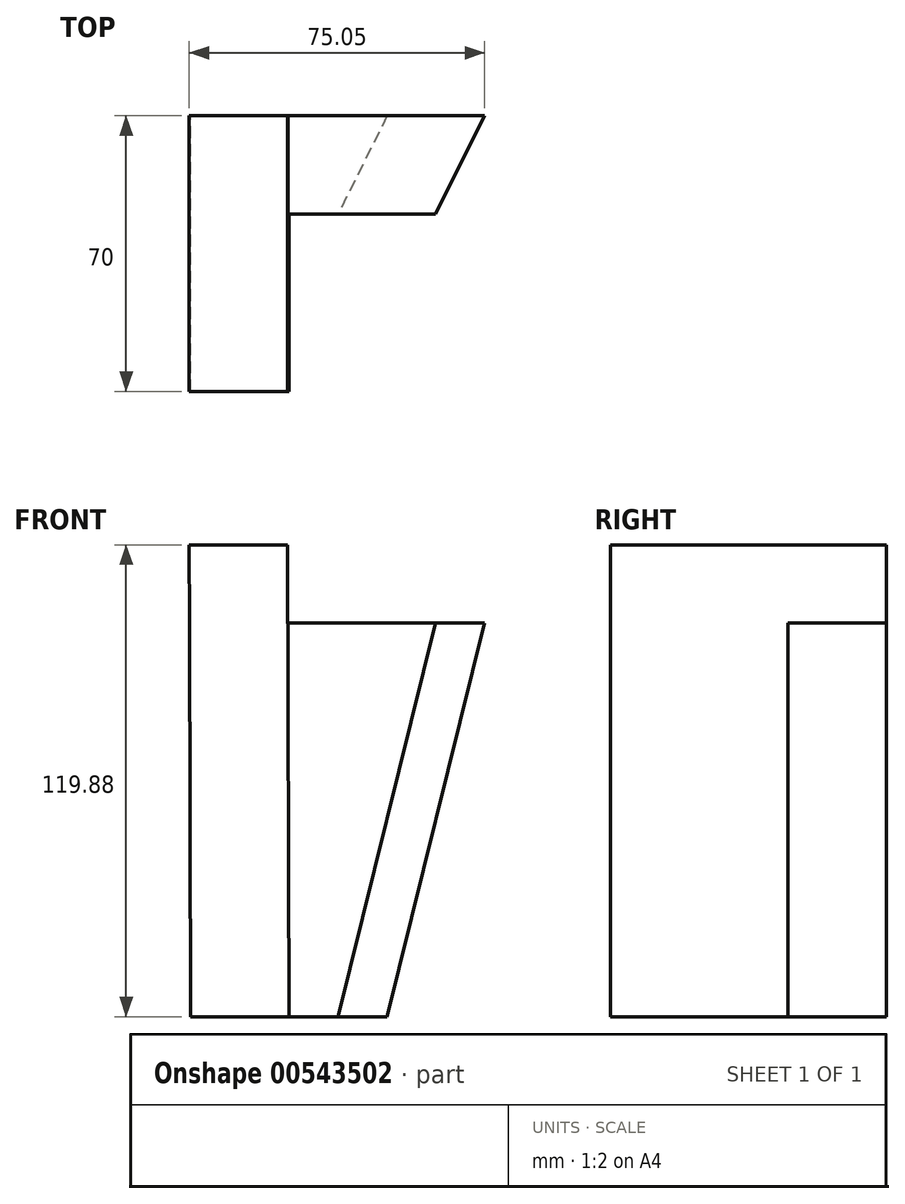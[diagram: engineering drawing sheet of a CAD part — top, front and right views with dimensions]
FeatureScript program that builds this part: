
annotation { "Feature Type Name" : "Feature", "Feature Type Description" : "" }
export const myFeature = defineFeature(function(context is Context, id is Id, definition is map)
    precondition{}
    {
        {
            var Q0;
            Q0=qCreatedBy(makeId("Top.planeOp"),FACE);
            cPlane(context, id + "F0", {"entities" : qUnion([Q0]), "cplaneType" : CPlaneType.OFFSET, "offset" : 100 * mm, "width" : 150 * mm, "height" : 150 * mm});
        }
        {
            var Q0;
            Q0=qCreatedBy(id+"F0.planeOp",FACE);
            var sketch = newSketch(context, id + "F1", { "sketchPlane" : qUnion([Q0])});
            skLineSegment(sketch, "E0", {"start": v(-31.5, -38.33) * mm, "end": v(-31.5, 31.67) * mm});
            skLineSegment(sketch, "E1", {"start": v(-31.5, 31.67) * mm, "end": v(43.5, 31.67) * mm});
            skLineSegment(sketch, "E2", {"start": v(43.5, 31.67) * mm, "end": v(31, 6.67) * mm});
            skLineSegment(sketch, "E3", {"start": v(31, 6.67) * mm, "end": v(-6.5, 6.67) * mm});
            skLineSegment(sketch, "E4", {"start": v(-6.5, 6.67) * mm, "end": v(-6.5, -38.33) * mm});
            skLineSegment(sketch, "E5", {"start": v(-6.5, -38.33) * mm, "end": v(-31.5, -38.33) * mm});
            skSolve(sketch);
        }
        {
            var Q0;
            Q0=qCreatedBy(makeId("Top.planeOp"),FACE);
            var sketch = newSketch(context, id + "F2", { "sketchPlane" : qUnion([Q0])});
            skLineSegment(sketch, "E6", {"start": v(-31.25, -38.33) * mm, "end": v(-31.25, 31.67) * mm});
            skLineSegment(sketch, "E7", {"start": v(-31.25, 31.67) * mm, "end": v(18.75, 31.67) * mm});
            skLineSegment(sketch, "E8", {"start": v(18.75, 31.67) * mm, "end": v(6.25, 6.67) * mm});
            skLineSegment(sketch, "E9", {"start": v(6.25, 6.67) * mm, "end": v(-6.25, 6.67) * mm});
            skLineSegment(sketch, "E10", {"start": v(-6.25, 6.67) * mm, "end": v(-6.25, -38.33) * mm});
            skLineSegment(sketch, "E11", {"start": v(-6.25, -38.33) * mm, "end": v(-31.25, -38.33) * mm});
            skSolve(sketch);
        }
        {
            var Q0;
            Q0 = qSketchRegion(id + "F2", true);
            var Q1;
            Q1 = qSketchRegion(id + "F1", true);
            loft(context, id + "F3", {"sheetProfilesArray" : [{ "sheetProfileEntities" : qUnion([Q0]) }, { "sheetProfileEntities" : qUnion([Q1]) }]});
        }
        {
            var Q0;
            Q0=makeQuery(id+"F3.opLoft","SWEPT_FACE",FACE,{"disambiguationData":[OSD([sQuery(id+"F1.wireOp",EDGE,"E3"),sQuery(id+"F1.wireOp",EDGE,"E4"),sQuery(id+"F1.wireOp",EDGE,"E5"),sQuery(id+"F2.wireOp",EDGE,"E9"),sQuery(id+"F2.wireOp",EDGE,"E10"),sQuery(id+"F2.wireOp",EDGE,"E11")])]});
            var sketch = newSketch(context, id + "F4", { "sketchPlane" : qUnion([Q0])});
            skLineSegment(sketch, "E12.bottom", {"start": v(-38.33, 119.9) * mm, "end": v(31.67, 119.9) * mm});
            skLineSegment(sketch, "E12.top", {"start": v(-38.33, 99.9) * mm, "end": v(31.67, 99.9) * mm});
            skLineSegment(sketch, "E12.left", {"start": v(-38.33, 119.9) * mm, "end": v(-38.33, 99.9) * mm});
            skLineSegment(sketch, "E12.right", {"start": v(31.67, 119.9) * mm, "end": v(31.67, 99.9) * mm});
            skSolve(sketch);
        }
        {
            var Q0;
            {var subQ4=sQuery(id+"F4.wireOp",EDGE,"E12.bottom");Q0=makeQuery(id+"F4.imprint","IMPRINT",FACE,{"disambiguationData":[TD([[makeQuery(id+"F4.imprint","IMPRINT",EDGE,{"derivedFrom":subQ4}),-1.0]])]});}
            extrude(context, id + "F5", {"entities" : qUnion([Q0]), "operationType" : NewBodyOperationType.ADD, "oppositeDirection" : true, "depth" : 25 * mm, "offsetDistance" : 25 * mm});
        }
        {
            var Q0;
            Q0=makeQuery(id+"F3.opLoft","SWEPT_FACE",FACE,{"disambiguationData":[OSD([sQuery(id+"F1.wireOp",EDGE,"E0"),sQuery(id+"F1.wireOp",EDGE,"E4"),sQuery(id+"F1.wireOp",EDGE,"E5"),sQuery(id+"F2.wireOp",EDGE,"E6"),sQuery(id+"F2.wireOp",EDGE,"E10"),sQuery(id+"F2.wireOp",EDGE,"E11")])]});
            var sketch = newSketch(context, id + "F6", { "sketchPlane" : qUnion([Q0])});
            skLineSegment(sketch, "E13.bottom", {"start": v(-6.5, 100) * mm, "end": v(-31.5, 100) * mm});
            skLineSegment(sketch, "E13.top", {"start": v(-6.5, 120) * mm, "end": v(-31.5, 120) * mm});
            skLineSegment(sketch, "E13.left", {"start": v(-6.5, 100) * mm, "end": v(-6.5, 120) * mm});
            skLineSegment(sketch, "E13.right", {"start": v(-31.5, 100) * mm, "end": v(-31.5, 120) * mm});
            skSolve(sketch);
        }
        {
            var Q0;
            Q0=makeQuery(id+"F3.opLoft","SWEPT_FACE",FACE,{"disambiguationData":[OSD([sQuery(id+"F1.wireOp",EDGE,"E0"),sQuery(id+"F1.wireOp",EDGE,"E1"),sQuery(id+"F1.wireOp",EDGE,"E2"),sQuery(id+"F2.wireOp",EDGE,"E6"),sQuery(id+"F2.wireOp",EDGE,"E7"),sQuery(id+"F2.wireOp",EDGE,"E8")])]});
            var sketch = newSketch(context, id + "F7", { "sketchPlane" : qUnion([Q0])});
            skLineSegment(sketch, "E14.bottom", {"start": v(6.54, 119.88) * mm, "end": v(31.5, 119.88) * mm});
            skLineSegment(sketch, "E14.top", {"start": v(6.54, 100) * mm, "end": v(31.5, 100) * mm});
            skLineSegment(sketch, "E14.left", {"start": v(6.54, 119.88) * mm, "end": v(6.54, 100) * mm});
            skLineSegment(sketch, "E14.right", {"start": v(31.5, 119.88) * mm, "end": v(31.5, 100) * mm});
            skSolve(sketch);
        }
    });
